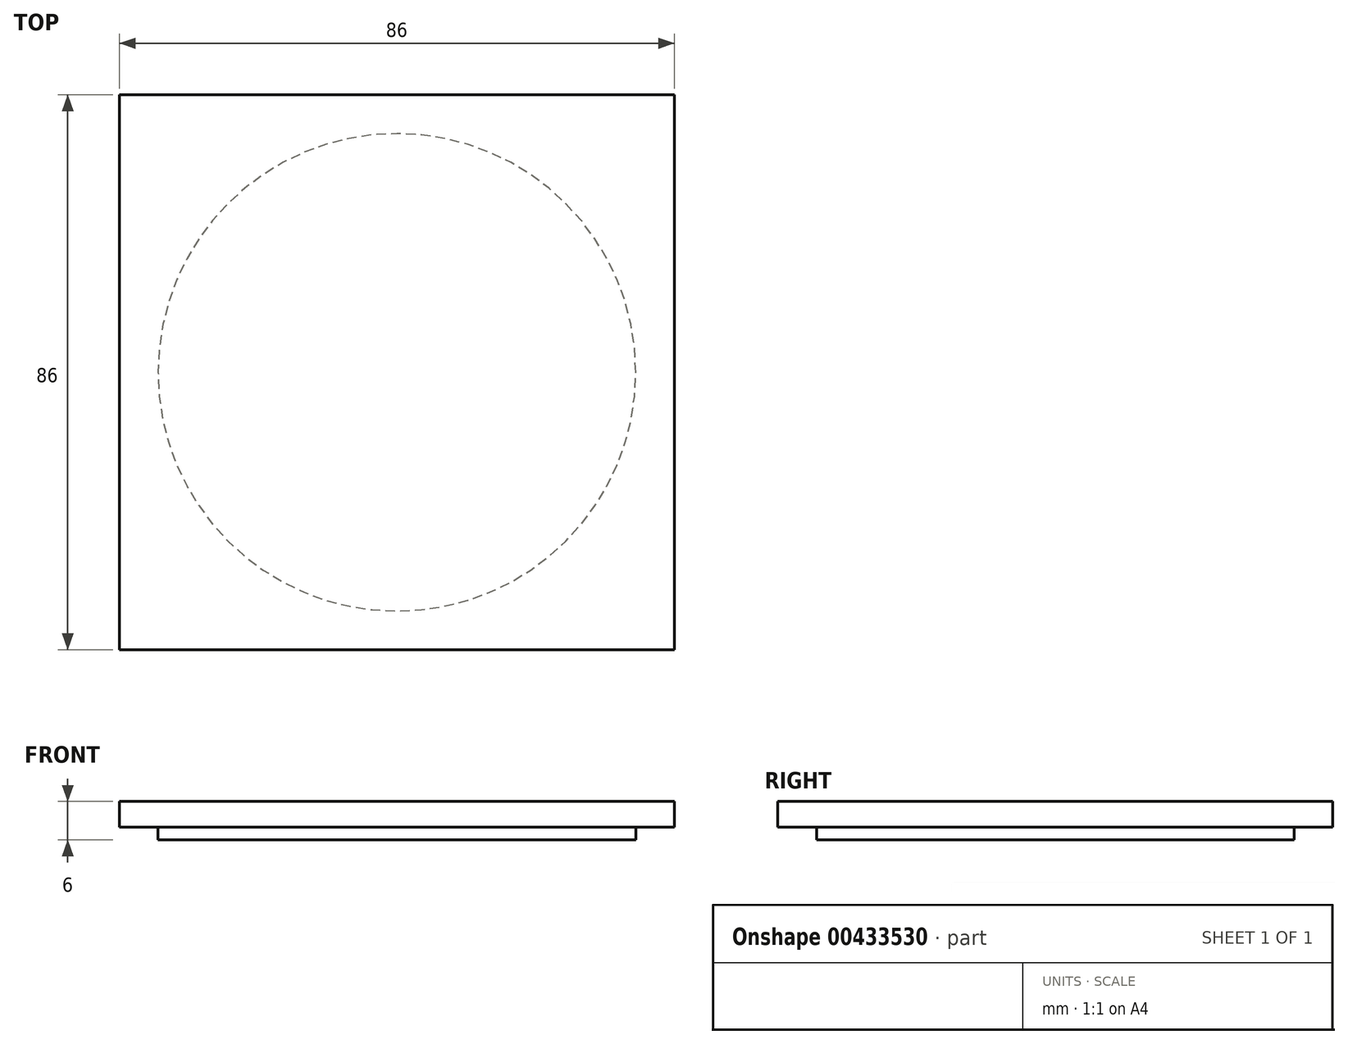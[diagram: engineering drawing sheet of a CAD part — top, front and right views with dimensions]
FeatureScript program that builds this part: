
annotation { "Feature Type Name" : "Feature", "Feature Type Description" : "" }
export const myFeature = defineFeature(function(context is Context, id is Id, definition is map)
    precondition{}
    {
        {
            var Q0;
            Q0=qCreatedBy(makeId("Top.planeOp"),FACE);
            var sketch = newSketch(context, id + "F0", { "sketchPlane" : qUnion([Q0])});
            skCircle(sketch, "E0", {"center": v(0, 0) * mm, "radius": 37 * mm});
            skLineSegment(sketch, "E1", {"start": v(0, 0) * mm, "end": v(0, -78.51) * mm, "construction": true});
            skLineSegment(sketch, "E2", {"start": v(0, 0) * mm, "end": v(106.74, 0) * mm, "construction": true});
            skLineSegment(sketch, "E3.bottom", {"start": v(43, -43) * mm, "end": v(-43, -43) * mm});
            skLineSegment(sketch, "E3.top", {"start": v(43, 43) * mm, "end": v(-43, 43) * mm});
            skLineSegment(sketch, "E3.left", {"start": v(43, -43) * mm, "end": v(43, 43) * mm});
            skLineSegment(sketch, "E3.right", {"start": v(-43, -43) * mm, "end": v(-43, 43) * mm});
            skCircle(sketch, "E4", {"center": v(0, 0) * mm, "radius": 48.5 * mm, "construction": true});
            skSolve(sketch);
        }
        {
            var Q0;
            Q0=makeQuery(id+"F0.imprint","IMPRINT",FACE,{"disambiguationData":[TD([[makeQuery(id+"F0.imprint","IMPRINT",EDGE,{"derivedFrom":sQuery(id+"F0.wireOp",EDGE,"E0")}),1.0]])]});
            var Q1;
            Q1=sQuery(id+"F0.wireOp",EDGE,"E0");
            extrude(context, id + "F1", {"entities" : qUnion([Q0]), "surfaceEntities" : qUnion([Q1]), "oppositeDirection" : true, "depth" : 2 * mm});
        }
        {
            var Q0;
            Q0=makeQuery(id+"F0.imprint","IMPRINT",FACE,{"disambiguationData":[TD([[makeQuery(id+"F0.imprint","IMPRINT",EDGE,{"derivedFrom":sQuery(id+"F0.wireOp",EDGE,"E0")}),-1.0]])]});
            var Q1;
            Q1=makeQuery(id+"F0.imprint","IMPRINT",FACE,{"disambiguationData":[TD([[makeQuery(id+"F0.imprint","IMPRINT",EDGE,{"derivedFrom":sQuery(id+"F0.wireOp",EDGE,"E0")}),1.0]])]});
            extrude(context, id + "F2", {"entities" : qUnion([Q0, Q1]), "operationType" : NewBodyOperationType.ADD, "depth" : 4 * mm});
        }
    });
